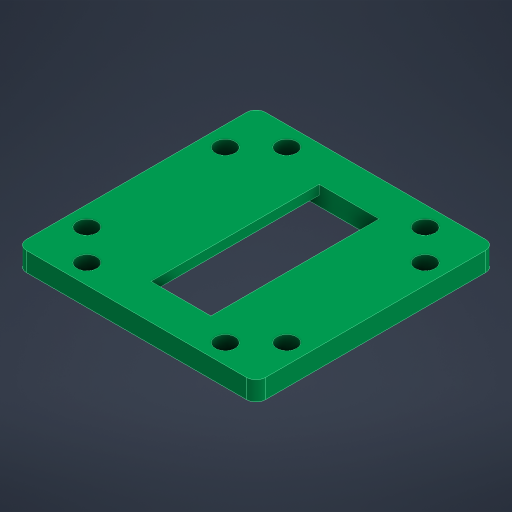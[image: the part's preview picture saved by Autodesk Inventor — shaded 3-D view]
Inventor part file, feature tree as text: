
AUTODESK INVENTOR PART (.ipt)
format: ipt  version: 2023.4 (Build 274418000, 418)  size: 258,560 bytes
history: native  units: mm
features: extrude x6, other x4, sketch x3, reference x2, plane x1, fillet x1, projected_geometry x1
ambient origin geometry x8: Origin, YZ Plane, XZ Plane, XY Plane, X Axis, Y Axis, Z Axis, Center Point
bodies: Solid1 (feature_tree)
feature tree (18):
  sketch  "Sketch1"  dims[d0=4.0mm d1=0.0mm d2=2.5mm]
  plane  "Work Plane1"
  extrude  "Extrusion1"  Depth=4.0mm
  sketch  "Sketch2"  dims[d3=4.25mm d4=2.125mm]
  extrude  "Extrusion2"  Depth=2.125mm
  extrude  "Extrusion3"  Depth=2.0mm TaperAngle=0.0deg
  extrude  "Extrusion4"  Depth=2.0mm TaperAngle=0.0deg
  fillet  "Fillet1"  Radius=2.0mm
  extrude  "Extrusion5"  Depth=2.0mm
  extrude  "Extrusion6"  Depth=2.0mm TaperAngle=0.0deg
  reference  "Reference1"
  projected_geometry  "Projected Loop1"
  sketch  "Sketch3"  dims[d5=2.0mm d6=0.0mm d7=2.0mm d8=0.0mm d9=49.8mm d10=0.0mm d11=2.0mm d12=5.0mm d13=49.8mm d14=0.0mm d15=0.125mm d16=7.5mm d17=7.5mm d18=2.0mm d19=0.0mm]
  reference  "Reference2"
  other  "<path>\Projects\Project Protocube\Protocube\CAD, STL, OBJ Files\1 CAD\Cube 1x1 V5.iam"
  other  "Cube 1x1 V5.iam"
  other  "Cube 1x1 Top V5 Closed Slotted:1"
  other  "Cube 1x1 Bottom V5 Closed Slotted:1"
note: 1 file-system path scrubbed to <path> (originals preserved in map.json)
